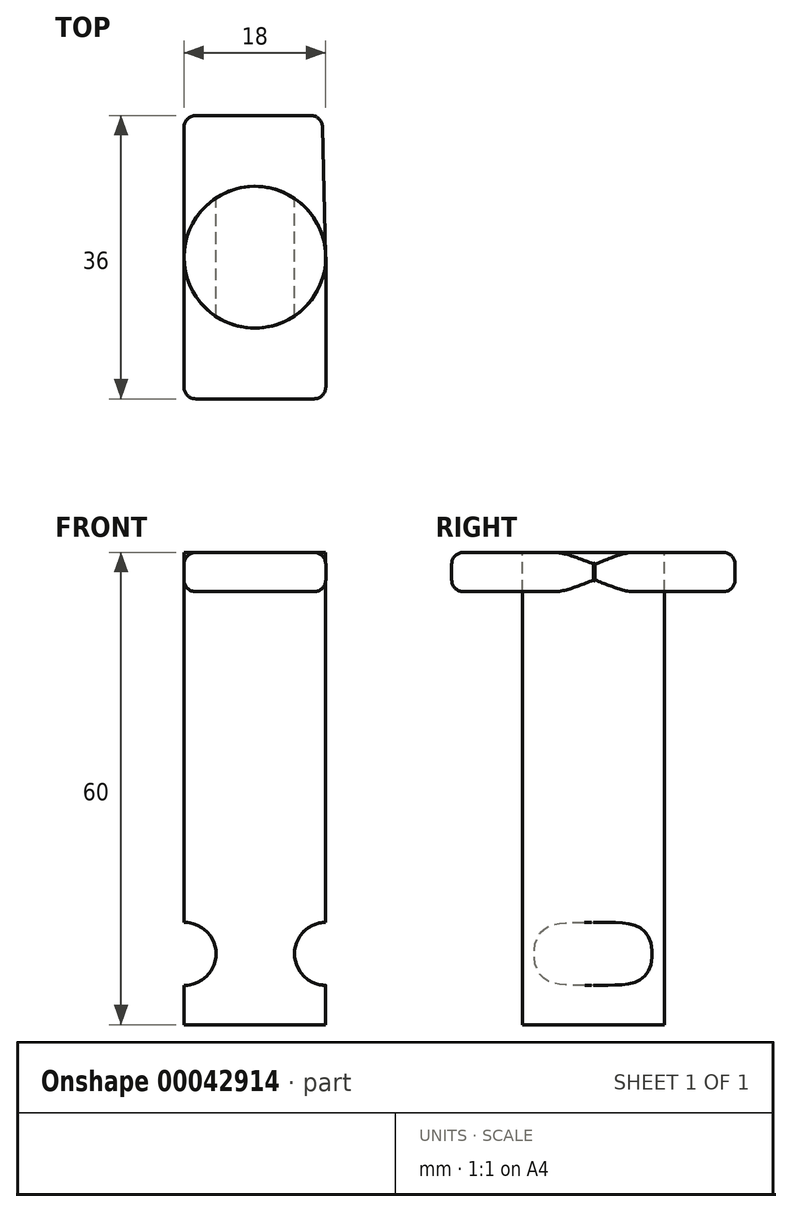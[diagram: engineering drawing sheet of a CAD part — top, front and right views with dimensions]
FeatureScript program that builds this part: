
annotation { "Feature Type Name" : "Feature", "Feature Type Description" : "" }
export const myFeature = defineFeature(function(context is Context, id is Id, definition is map)
    precondition{}
    {
        {
            var Q0;
            Q0=qCreatedBy(makeId("Top.planeOp"),FACE);
            var sketch = newSketch(context, id + "F0", { "sketchPlane" : qUnion([Q0])});
            skCircle(sketch, "E0", {"center": v(0, 0) * mm, "radius": 9 * mm});
            skCircle(sketch, "E1", {"center": v(0, 0) * mm, "radius": 15 * mm});
            skSolve(sketch);
        }
        {
            var Q0;
            Q0=makeQuery(id+"F0.imprint","IMPRINT",FACE,{"disambiguationData":[TD([[makeQuery(id+"F0.imprint","IMPRINT",EDGE,{"derivedFrom":sQuery(id+"F0.wireOp",EDGE,"E0")}),1.0]])]});
            extrude(context, id + "F1", {"entities" : qUnion([Q0]), "depth" : 60 * mm});
        }
        {
            var Q0;
            Q0=qCreatedBy(makeId("Front.planeOp"),FACE);
            var sketch = newSketch(context, id + "F2", { "sketchPlane" : qUnion([Q0])});
            skCircle(sketch, "E2", {"center": v(9.03, 9) * mm, "radius": 4 * mm});
            skCircle(sketch, "E3", {"center": v(-8.93, 9) * mm, "radius": 4 * mm});
            skSolve(sketch);
        }
        {
            var Q0;
            Q0=makeQuery(id+"F2.imprint","IMPRINT",FACE,{"disambiguationData":[TD([[makeQuery(id+"F2.imprint","IMPRINT",EDGE,{"derivedFrom":sQuery(id+"F2.wireOp",EDGE,"E3")}),1.0]])]});
            var Q1;
            Q1=makeQuery(id+"F2.imprint","IMPRINT",FACE,{"disambiguationData":[TD([[makeQuery(id+"F2.imprint","IMPRINT",EDGE,{"derivedFrom":sQuery(id+"F2.wireOp",EDGE,"E2")}),1.0]])]});
            extrude(context, id + "F3", {"entities" : qUnion([Q0, Q1]), "operationType" : NewBodyOperationType.REMOVE, "depth" : 12.55 * mm, "hasSecondDirection" : true, "secondDirectionOppositeDirection" : true, "secondDirectionDepth" : 46.04 * mm});
        }
        {
            var Q0;
            Q0=makeQuery(id+"F1.opExtrude","CAP_FACE",FACE,{"disambiguationData":[OSD([sQuery(id+"F0.wireOp",EDGE,"E0")])],"isStart":false});
            var sketch = newSketch(context, id + "F4", { "sketchPlane" : qUnion([Q0])});
            skLineSegment(sketch, "E4", {"start": v(-9, 0) * mm, "end": v(-9, 18) * mm});
            skLineSegment(sketch, "E5", {"start": v(-9, 18) * mm, "end": v(8.56, 18) * mm});
            skLineSegment(sketch, "E6", {"start": v(8.56, 18) * mm, "end": v(9, 0) * mm});
            skLineSegment(sketch, "E7", {"start": v(9, 0) * mm, "end": v(9, -18) * mm});
            skLineSegment(sketch, "E8", {"start": v(9, -18) * mm, "end": v(-9, -18) * mm});
            skLineSegment(sketch, "E9", {"start": v(-9, -18) * mm, "end": v(-9, 0) * mm});
            skPoint(sketch, "E10.centerSnap0", {"position": v(0, -18) * mm});
            skSolve(sketch);
        }
        {
            var Q0;
            {var subQ1=sQuery(id+"F4.wireOp",EDGE,"E7");Q0=makeQuery(id+"F4.imprint","IMPRINT",FACE,{"disambiguationData":[TD([[makeQuery(id+"F4.imprint","IMPRINT",EDGE,{"derivedFrom":subQ1}),-1.0]])]});}
            var Q1;
            {var subQ0=sQuery(id+"F4.wireOp",EDGE,"E4");Q1=makeQuery(id+"F4.imprint","IMPRINT",FACE,{"disambiguationData":[TD([[makeQuery(id+"F4.imprint","IMPRINT",EDGE,{"derivedFrom":subQ0}),-1.0]])]});}
            extrude(context, id + "F5", {"entities" : qUnion([Q0, Q1]), "oppositeDirection" : true, "depth" : 5 * mm});
        }
        {
            var Q0;
            Q0=makeQuery(id+"F5.opExtrude","CAP_EDGE",EDGE,{"disambiguationData":[OSD([sQuery(id+"F4.wireOp",EDGE,"E9")])],"isStart":true});
            var Q1;
            Q1=makeQuery(id+"F5.opExtrude","CAP_EDGE",EDGE,{"disambiguationData":[OSD([sQuery(id+"F4.wireOp",EDGE,"E4")])],"isStart":true});
            var Q2;
            Q2=makeQuery(id+"F5.opExtrude","CAP_EDGE",EDGE,{"disambiguationData":[OSD([sQuery(id+"F4.wireOp",EDGE,"E5")])],"isStart":true});
            var Q3;
            {var subQ0=sQuery(id+"F4.wireOp",EDGE,"E6");Q3=makeQuery(id+"F5.opExtrude","CAP_EDGE",EDGE,{"disambiguationData":[OSD([subQ0]),TDD([makeQuery(id+"F4.imprint","IMPRINT",EDGE,{"disambiguationData":[TD([[makeQuery(id+"F4.imprint","INTERSECT",VERTEX,{"derivedFrom":[sQuery(id+"F4.wireOp",EDGE,"E5"),subQ0]}),-1.0]])],"derivedFrom":subQ0})])],"isStart":true});}
            var Q4;
            Q4=makeQuery(id+"F5.opExtrude","CAP_EDGE",EDGE,{"disambiguationData":[OSD([sQuery(id+"F4.wireOp",EDGE,"E7")])],"isStart":true});
            var Q5;
            Q5=makeQuery(id+"F5.opExtrude","CAP_EDGE",EDGE,{"disambiguationData":[OSD([sQuery(id+"F4.wireOp",EDGE,"E8")])],"isStart":true});
            var Q6;
            Q6=makeQuery(id+"F5.opExtrude","SWEPT_EDGE",EDGE,{"disambiguationData":[OSD([sQuery(id+"F4.wireOp",EDGE,"E4"),sQuery(id+"F4.wireOp",EDGE,"E5")])]});
            var Q7;
            Q7=makeQuery(id+"F5.opExtrude","CAP_EDGE",EDGE,{"disambiguationData":[OSD([sQuery(id+"F4.wireOp",EDGE,"E5")])],"isStart":false});
            var Q8;
            Q8=makeQuery(id+"F5.opExtrude","SWEPT_EDGE",EDGE,{"disambiguationData":[OSD([sQuery(id+"F4.wireOp",EDGE,"E5"),sQuery(id+"F4.wireOp",EDGE,"E6")])]});
            var Q9;
            Q9=makeQuery(id+"F5.opExtrude","CAP_EDGE",EDGE,{"disambiguationData":[OSD([sQuery(id+"F4.wireOp",EDGE,"E4")])],"isStart":false});
            var Q10;
            Q10=makeQuery(id+"F5.opExtrude","CAP_EDGE",EDGE,{"disambiguationData":[OSD([sQuery(id+"F4.wireOp",EDGE,"E9")])],"isStart":false});
            var Q11;
            {var subQ0=sQuery(id+"F4.wireOp",EDGE,"E6");Q11=makeQuery(id+"F5.opExtrude","CAP_EDGE",EDGE,{"disambiguationData":[OSD([subQ0]),TDD([makeQuery(id+"F4.imprint","IMPRINT",EDGE,{"disambiguationData":[TD([[makeQuery(id+"F4.imprint","INTERSECT",VERTEX,{"derivedFrom":[sQuery(id+"F4.wireOp",EDGE,"E5"),subQ0]}),-1.0]])],"derivedFrom":subQ0})])],"isStart":false});}
            var Q12;
            Q12=makeQuery(id+"F5.opExtrude","CAP_EDGE",EDGE,{"disambiguationData":[OSD([sQuery(id+"F4.wireOp",EDGE,"E8")])],"isStart":false});
            var Q13;
            Q13=makeQuery(id+"F5.opExtrude","SWEPT_EDGE",EDGE,{"disambiguationData":[OSD([sQuery(id+"F4.wireOp",EDGE,"E7"),sQuery(id+"F4.wireOp",EDGE,"E8")])]});
            var Q14;
            Q14=makeQuery(id+"F5.opExtrude","SWEPT_EDGE",EDGE,{"disambiguationData":[OSD([sQuery(id+"F4.wireOp",EDGE,"E8"),sQuery(id+"F4.wireOp",EDGE,"E9")])]});
            var Q15;
            Q15=makeQuery(id+"F5.opExtrude","CAP_EDGE",EDGE,{"disambiguationData":[OSD([sQuery(id+"F4.wireOp",EDGE,"E7")])],"isStart":false});
            fillet(context, id + "F6", {"entities" : qUnion([Q0, Q1, Q2, Q3, Q4, Q5, Q6, Q7, Q8, Q9, Q10, Q11, Q12, Q13, Q14, Q15]), "radius" : 1.5 * mm, "tangentPropagation" : true, "allowEdgeOverflow" : false});
        }
    });
